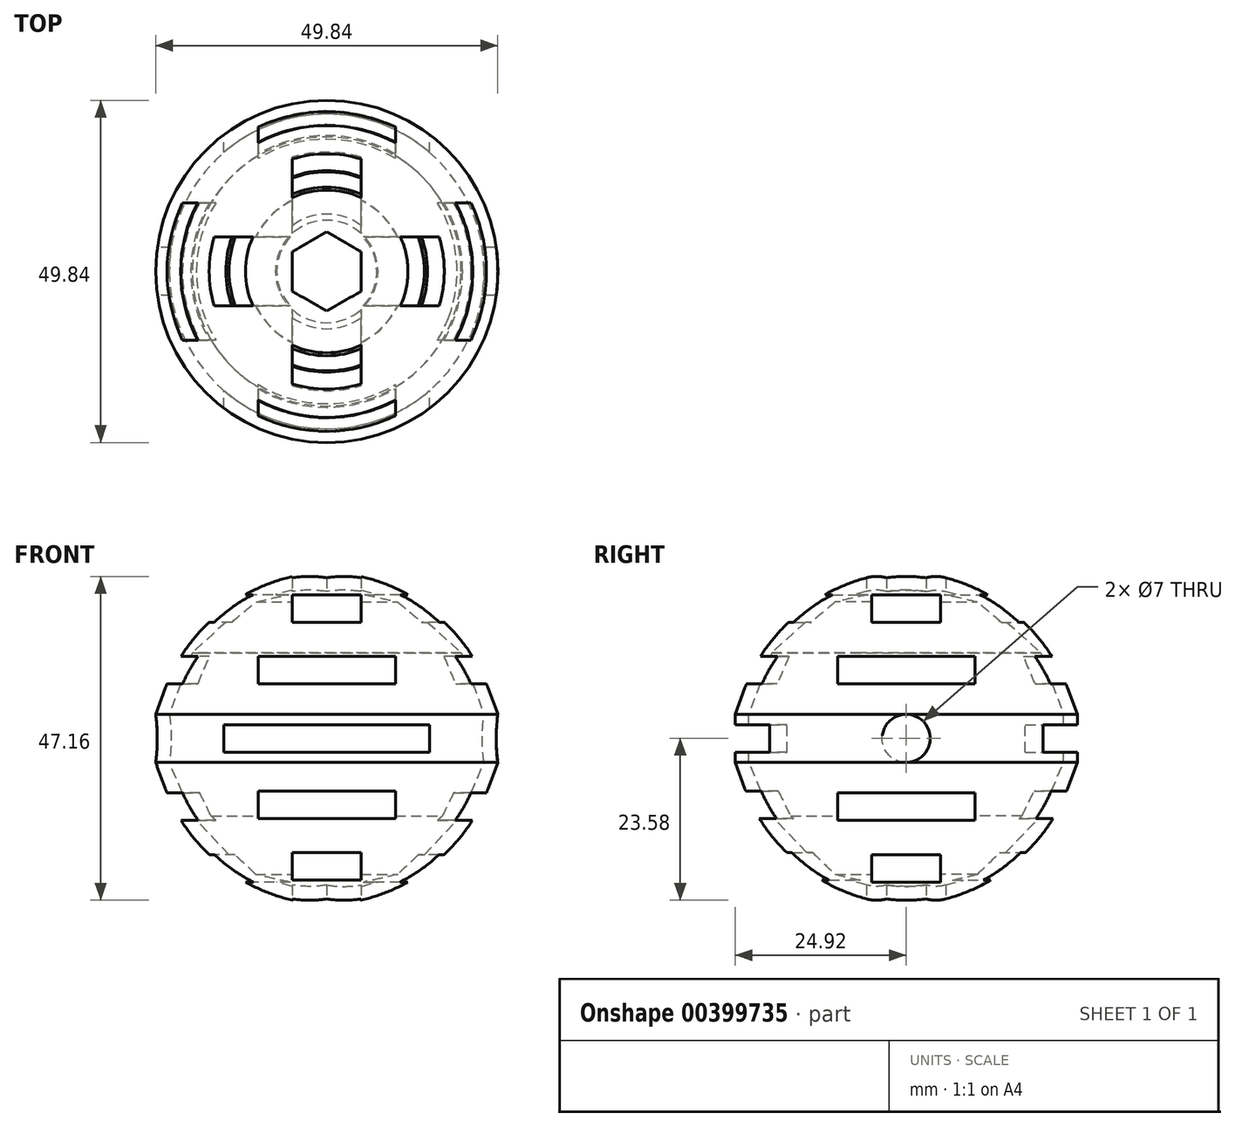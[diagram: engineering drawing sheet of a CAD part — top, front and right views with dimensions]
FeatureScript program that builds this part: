
annotation { "Feature Type Name" : "Feature", "Feature Type Description" : "" }
export const myFeature = defineFeature(function(context is Context, id is Id, definition is map)
    precondition{}
    {
        {
            var Q0;
            Q0=qCreatedBy(makeId("Top.planeOp"),FACE);
            var sketch = newSketch(context, id + "F0", { "sketchPlane" : qUnion([Q0])});
            skCircle(sketch, "E0", {"center": v(0, 0) * mm, "radius": 25 * mm});
            skSolve(sketch);
        }
        {
            var Q0;
            Q0=qCreatedBy(makeId("Front.planeOp"),FACE);
            var sketch = newSketch(context, id + "F1", { "sketchPlane" : qUnion([Q0])});
            skLineSegment(sketch, "E1", {"start": v(0, -24.65) * mm, "end": v(0, 24.92) * mm});
            skArc(sketch, "E2", {"start": v(0, 24.92) * mm, "mid": v(-24.92, 0) * mm, "end": v(0, -24.92) * mm});
            skLineSegment(sketch, "E3", {"start": v(0, 24.92) * mm, "end": v(0, -24.65) * mm});
            skSolve(sketch);
        }
        {
            var Q0;
            Q0=qCreatedBy(makeId("Top.planeOp"),FACE);
            var sketch = newSketch(context, id + "F2", { "sketchPlane" : qUnion([Q0])});
            skLineSegment(sketch, "E4", {"start": v(0, 25) * mm, "end": v(0, -25) * mm});
            skSolve(sketch);
        }
        {
            var Q0;
            Q0=qCreatedBy(makeId("Front.planeOp"),FACE);
            var sketch = newSketch(context, id + "F3", { "sketchPlane" : qUnion([Q0])});
            skLineSegment(sketch, "E5", {"start": v(-12.52, -21.55) * mm, "end": v(15.6, 27.16) * mm});
            skLineSegment(sketch, "E6", {"start": v(-21.58, -12.46) * mm, "end": v(24.24, 14) * mm});
            skLineSegment(sketch, "E7", {"start": v(-21.58, 12.46) * mm, "end": v(18.12, -10.46) * mm});
            skLineSegment(sketch, "E8", {"start": v(-12.46, 21.58) * mm, "end": v(12.77, -22.11) * mm});
            skLineSegment(sketch, "E9.bottom", {"start": v(-24.92, 3.5) * mm, "end": v(24.92, 3.5) * mm});
            skLineSegment(sketch, "E9.top", {"start": v(-24.92, -3.5) * mm, "end": v(24.92, -3.5) * mm});
            skLineSegment(sketch, "E9.left", {"start": v(-24.92, 3.5) * mm, "end": v(-24.92, -3.5) * mm});
            skLineSegment(sketch, "E9.right", {"start": v(24.92, 3.5) * mm, "end": v(24.92, -3.5) * mm});
            skPoint(sketch, "E9.middle", {"position": v(0, 0) * mm});
            skSolve(sketch);
        }
        {
            var Q0;
            Q0=qCreatedBy(makeId("Front.planeOp"),FACE);
            var sketch = newSketch(context, id + "F4", { "sketchPlane" : qUnion([Q0])});
            skLineSegment(sketch, "E10", {"start": v(0, -24.94) * mm, "end": v(-12.46, -21.55) * mm});
            skLineSegment(sketch, "E11", {"start": v(-12.46, -21.55) * mm, "end": v(-21.58, -12.46) * mm});
            skLineSegment(sketch, "E12", {"start": v(-21.58, -12.46) * mm, "end": v(-24.92, -3.5) * mm});
            skLineSegment(sketch, "E13", {"start": v(-24.92, -3.5) * mm, "end": v(-24.92, 3.5) * mm});
            skLineSegment(sketch, "E14", {"start": v(-24.92, 3.5) * mm, "end": v(-21.58, 12.46) * mm});
            skLineSegment(sketch, "E15", {"start": v(-21.58, 12.46) * mm, "end": v(-12.46, 21.58) * mm});
            skLineSegment(sketch, "E16", {"start": v(-12.46, 21.58) * mm, "end": v(0, 24.92) * mm});
            skLineSegment(sketch, "E17", {"start": v(0, 24.92) * mm, "end": v(0, -24.94) * mm});
            skSolve(sketch);
        }
        {
            var Q0;
            Q0=qCreatedBy(makeId("Front.planeOp"),FACE);
            var sketch = newSketch(context, id + "F5", { "sketchPlane" : qUnion([Q0])});
            skLineSegment(sketch, "E18", {"start": v(0, 37.91) * mm, "end": v(0, 29) * mm});
            skSolve(sketch);
        }
        {
            var Q0;
            Q0=qCreatedBy(makeId("Front.planeOp"),FACE);
            var sketch = newSketch(context, id + "F6", { "sketchPlane" : qUnion([Q0])});
            skLineSegment(sketch, "E19", {"start": v(0, -22.92) * mm, "end": v(-11.5, -19.8) * mm});
            skLineSegment(sketch, "E20", {"start": v(-11.5, -19.8) * mm, "end": v(-19.58, -11.3) * mm});
            skLineSegment(sketch, "E21", {"start": v(-19.58, -11.3) * mm, "end": v(-22.92, -3.5) * mm});
            skLineSegment(sketch, "E22", {"start": v(-22.92, -3.5) * mm, "end": v(-22.92, 3.5) * mm});
            skLineSegment(sketch, "E23", {"start": v(-22.92, 3.5) * mm, "end": v(-19.58, 12.46) * mm});
            skLineSegment(sketch, "E24", {"start": v(-19.58, 12.46) * mm, "end": v(-11.46, 19.85) * mm});
            skLineSegment(sketch, "E25", {"start": v(-11.46, 19.85) * mm, "end": v(0, 22.92) * mm});
            skLineSegment(sketch, "E26", {"start": v(0, 22.92) * mm, "end": v(0, -22.92) * mm});
            skSolve(sketch);
        }
        {
            var Q0;
            Q0 = qSketchRegion(id + "F4", true);
            var Q1;
            Q1=sQuery(id+"F5.wireOp",EDGE,"E18");
            revolve(context, id + "F7", {"entities" : qUnion([Q0]), "axis" : qUnion([Q1]), "revolveType" : RevolveType.FULL});
        }
        {
            var Q0;
            Q0 = qSketchRegion(id + "F6", true);
            var Q1;
            Q1=sQuery(id+"F5.wireOp",EDGE,"E18");
            revolve(context, id + "F8", {"operationType" : NewBodyOperationType.REMOVE, "entities" : qUnion([Q0]), "axis" : qUnion([Q1]), "revolveType" : RevolveType.FULL});
        }
        {
            var Q0;
            Q0=qCreatedBy(makeId("Right.planeOp"),FACE);
            var sketch = newSketch(context, id + "F9", { "sketchPlane" : qUnion([Q0])});
            skCircle(sketch, "E27", {"center": v(0, 0) * mm, "radius": 3.5 * mm});
            skSolve(sketch);
        }
        {
            var Q0;
            Q0 = qSketchRegion(id + "F9", true);
            extrude(context, id + "F10", {"entities" : qUnion([Q0]), "operationType" : NewBodyOperationType.REMOVE, "depth" : 30 * mm, "hasSecondDirection" : true, "secondDirectionOppositeDirection" : true, "secondDirectionDepth" : 30 * mm});
        }
        {
            var Q0;
            Q0=makeQuery(id+"F7.opRevolve","SWEPT_EDGE",EDGE,{"disambiguationData":[OSD([sQuery(id+"F4.wireOp",EDGE,"E14"),sQuery(id+"F4.wireOp",EDGE,"E15")])]});
            var Q1;
            Q1=makeQuery(id+"F7.opRevolve","SWEPT_EDGE",EDGE,{"disambiguationData":[OSD([sQuery(id+"F4.wireOp",EDGE,"E11"),sQuery(id+"F4.wireOp",EDGE,"E12")])]});
            var Q2;
            Q2=makeQuery(id+"F7.opRevolve","SWEPT_EDGE",EDGE,{"disambiguationData":[OSD([sQuery(id+"F4.wireOp",EDGE,"E10"),sQuery(id+"F4.wireOp",EDGE,"E11")])]});
            var Q3;
            Q3=makeQuery(id+"F7.opRevolve","SWEPT_EDGE",EDGE,{"disambiguationData":[OSD([sQuery(id+"F4.wireOp",EDGE,"E15"),sQuery(id+"F4.wireOp",EDGE,"E16")])]});
            fillet(context, id + "F11", {"entities" : qUnion([Q0, Q1, Q2, Q3]), "radius" : 25 * mm, "tangentPropagation" : true, "allowEdgeOverflow" : false});
        }
        {
            var Q0;
            Q0=qCreatedBy(makeId("Front.planeOp"),FACE);
            var sketch = newSketch(context, id + "F12", { "sketchPlane" : qUnion([Q0])});
            skLineSegment(sketch, "E28.bottom", {"start": v(-5, 20.92) * mm, "end": v(5, 20.92) * mm});
            skLineSegment(sketch, "E28.top", {"start": v(-5, 16.92) * mm, "end": v(5, 16.92) * mm});
            skLineSegment(sketch, "E28.left", {"start": v(-5, 20.92) * mm, "end": v(-5, 16.92) * mm});
            skLineSegment(sketch, "E28.right", {"start": v(5, 20.92) * mm, "end": v(5, 16.92) * mm});
            skPoint(sketch, "E28.middle", {"position": v(0, 18.92) * mm});
            skLineSegment(sketch, "E29.bottom", {"start": v(-10, 11.92) * mm, "end": v(10, 11.92) * mm});
            skLineSegment(sketch, "E29.top", {"start": v(-10, 7.92) * mm, "end": v(10, 7.92) * mm});
            skLineSegment(sketch, "E29.left", {"start": v(-10, 11.92) * mm, "end": v(-10, 7.92) * mm});
            skLineSegment(sketch, "E29.right", {"start": v(10, 11.92) * mm, "end": v(10, 7.92) * mm});
            skPoint(sketch, "E29.middle", {"position": v(0, 9.92) * mm});
            skLineSegment(sketch, "E30.bottom", {"start": v(-5, -16.65) * mm, "end": v(5, -16.65) * mm});
            skLineSegment(sketch, "E30.top", {"start": v(-5, -20.65) * mm, "end": v(5, -20.65) * mm});
            skLineSegment(sketch, "E30.left", {"start": v(-5, -16.65) * mm, "end": v(-5, -20.65) * mm});
            skLineSegment(sketch, "E30.right", {"start": v(5, -16.65) * mm, "end": v(5, -20.65) * mm});
            skPoint(sketch, "E30.middle", {"position": v(0, -18.65) * mm});
            skLineSegment(sketch, "E31.bottom", {"start": v(-5, -7.65) * mm, "end": v(5, -7.65) * mm});
            skLineSegment(sketch, "E31.top", {"start": v(-5, -11.65) * mm, "end": v(5, -11.65) * mm});
            skLineSegment(sketch, "E31.left", {"start": v(-5, -7.65) * mm, "end": v(-5, -11.65) * mm});
            skLineSegment(sketch, "E31.right", {"start": v(5, -7.65) * mm, "end": v(5, -11.65) * mm});
            skPoint(sketch, "E31.middle", {"position": v(0, -9.65) * mm});
            skLineSegment(sketch, "E32.bottom", {"start": v(-15, 2) * mm, "end": v(15, 2) * mm});
            skLineSegment(sketch, "E32.top", {"start": v(-15, -2) * mm, "end": v(15, -2) * mm});
            skLineSegment(sketch, "E32.left", {"start": v(-15, 2) * mm, "end": v(-15, -2) * mm});
            skLineSegment(sketch, "E32.right", {"start": v(15, 2) * mm, "end": v(15, -2) * mm});
            skPoint(sketch, "E32.middle", {"position": v(0, 0) * mm});
            skLineSegment(sketch, "E33.bottom", {"start": v(-10, -7.65) * mm, "end": v(10, -7.65) * mm});
            skLineSegment(sketch, "E33.top", {"start": v(-10, -11.65) * mm, "end": v(10, -11.65) * mm});
            skLineSegment(sketch, "E33.left", {"start": v(-10, -7.65) * mm, "end": v(-10, -11.65) * mm});
            skLineSegment(sketch, "E33.right", {"start": v(10, -7.65) * mm, "end": v(10, -11.65) * mm});
            skSolve(sketch);
        }
        {
            var Q0;
            Q0 = qSketchRegion(id + "F12", true);
            extrude(context, id + "F13", {"entities" : qUnion([Q0]), "operationType" : NewBodyOperationType.REMOVE, "depth" : 30 * mm, "hasSecondDirection" : true, "secondDirectionOppositeDirection" : true, "secondDirectionDepth" : 30 * mm});
        }
        {
            var Q0;
            Q0=qCreatedBy(makeId("Right.planeOp"),FACE);
            var sketch = newSketch(context, id + "F14", { "sketchPlane" : qUnion([Q0])});
            skLineSegment(sketch, "E34.bottom", {"start": v(5, 20.92) * mm, "end": v(-5, 20.92) * mm});
            skLineSegment(sketch, "E34.top", {"start": v(5, 16.92) * mm, "end": v(-5, 16.92) * mm});
            skLineSegment(sketch, "E34.left", {"start": v(5, 20.92) * mm, "end": v(5, 16.92) * mm});
            skLineSegment(sketch, "E34.right", {"start": v(-5, 20.92) * mm, "end": v(-5, 16.92) * mm});
            skPoint(sketch, "E34.middle", {"position": v(0, 18.92) * mm});
            skLineSegment(sketch, "E35.bottom", {"start": v(10, 11.92) * mm, "end": v(-10, 11.92) * mm});
            skLineSegment(sketch, "E35.top", {"start": v(10, 7.92) * mm, "end": v(-10, 7.92) * mm});
            skLineSegment(sketch, "E35.left", {"start": v(10, 11.92) * mm, "end": v(10, 7.92) * mm});
            skLineSegment(sketch, "E35.right", {"start": v(-10, 11.92) * mm, "end": v(-10, 7.92) * mm});
            skPoint(sketch, "E35.middle", {"position": v(0, 9.92) * mm});
            skLineSegment(sketch, "E36.bottom", {"start": v(10, -7.94) * mm, "end": v(-10, -7.94) * mm});
            skLineSegment(sketch, "E36.top", {"start": v(10, -11.94) * mm, "end": v(-10, -11.94) * mm});
            skLineSegment(sketch, "E36.left", {"start": v(10, -7.94) * mm, "end": v(10, -11.94) * mm});
            skLineSegment(sketch, "E36.right", {"start": v(-10, -7.94) * mm, "end": v(-10, -11.94) * mm});
            skPoint(sketch, "E36.middle", {"position": v(0, -9.94) * mm});
            skLineSegment(sketch, "E37.bottom", {"start": v(5, -16.94) * mm, "end": v(-5, -16.94) * mm});
            skLineSegment(sketch, "E37.top", {"start": v(5, -20.94) * mm, "end": v(-5, -20.94) * mm});
            skLineSegment(sketch, "E37.left", {"start": v(5, -16.94) * mm, "end": v(5, -20.94) * mm});
            skLineSegment(sketch, "E37.right", {"start": v(-5, -16.94) * mm, "end": v(-5, -20.94) * mm});
            skPoint(sketch, "E37.middle", {"position": v(0, -18.94) * mm});
            skSolve(sketch);
        }
        {
            var Q0;
            Q0 = qSketchRegion(id + "F14", true);
            extrude(context, id + "F15", {"entities" : qUnion([Q0]), "operationType" : NewBodyOperationType.REMOVE, "depth" : 30 * mm, "hasSecondDirection" : true, "secondDirectionOppositeDirection" : true, "secondDirectionDepth" : 30 * mm});
        }
        {
            var Q0;
            Q0=qCreatedBy(makeId("Top.planeOp"),FACE);
            var sketch = newSketch(context, id + "F16", { "sketchPlane" : qUnion([Q0])});
            skCircle(sketch, "E38.cCircle", {"center": v(0, 0) * mm, "radius": 5 * mm, "construction": true});
            skLineSegment(sketch, "E38.0", {"start": v(0, 5.77) * mm, "end": v(5, 2.89) * mm});
            skLineSegment(sketch, "E38.1", {"start": v(5, 2.89) * mm, "end": v(5, -2.89) * mm});
            skLineSegment(sketch, "E38.2", {"start": v(5, -2.89) * mm, "end": v(0, -5.77) * mm});
            skLineSegment(sketch, "E38.3", {"start": v(0, -5.77) * mm, "end": v(-5, -2.89) * mm});
            skLineSegment(sketch, "E38.4", {"start": v(-5, -2.89) * mm, "end": v(-5, 2.89) * mm});
            skLineSegment(sketch, "E38.5", {"start": v(-5, 2.89) * mm, "end": v(0, 5.77) * mm});
            skPoint(sketch, "E38.0.midPoint", {"position": v(2.5, 4.33) * mm});
            skSolve(sketch);
        }
        {
            var Q0;
            Q0 = qSketchRegion(id + "F16", true);
            extrude(context, id + "F17", {"entities" : qUnion([Q0]), "operationType" : NewBodyOperationType.REMOVE, "depth" : 30 * mm, "hasSecondDirection" : true, "secondDirectionOppositeDirection" : true, "secondDirectionDepth" : 30 * mm});
        }
    });
